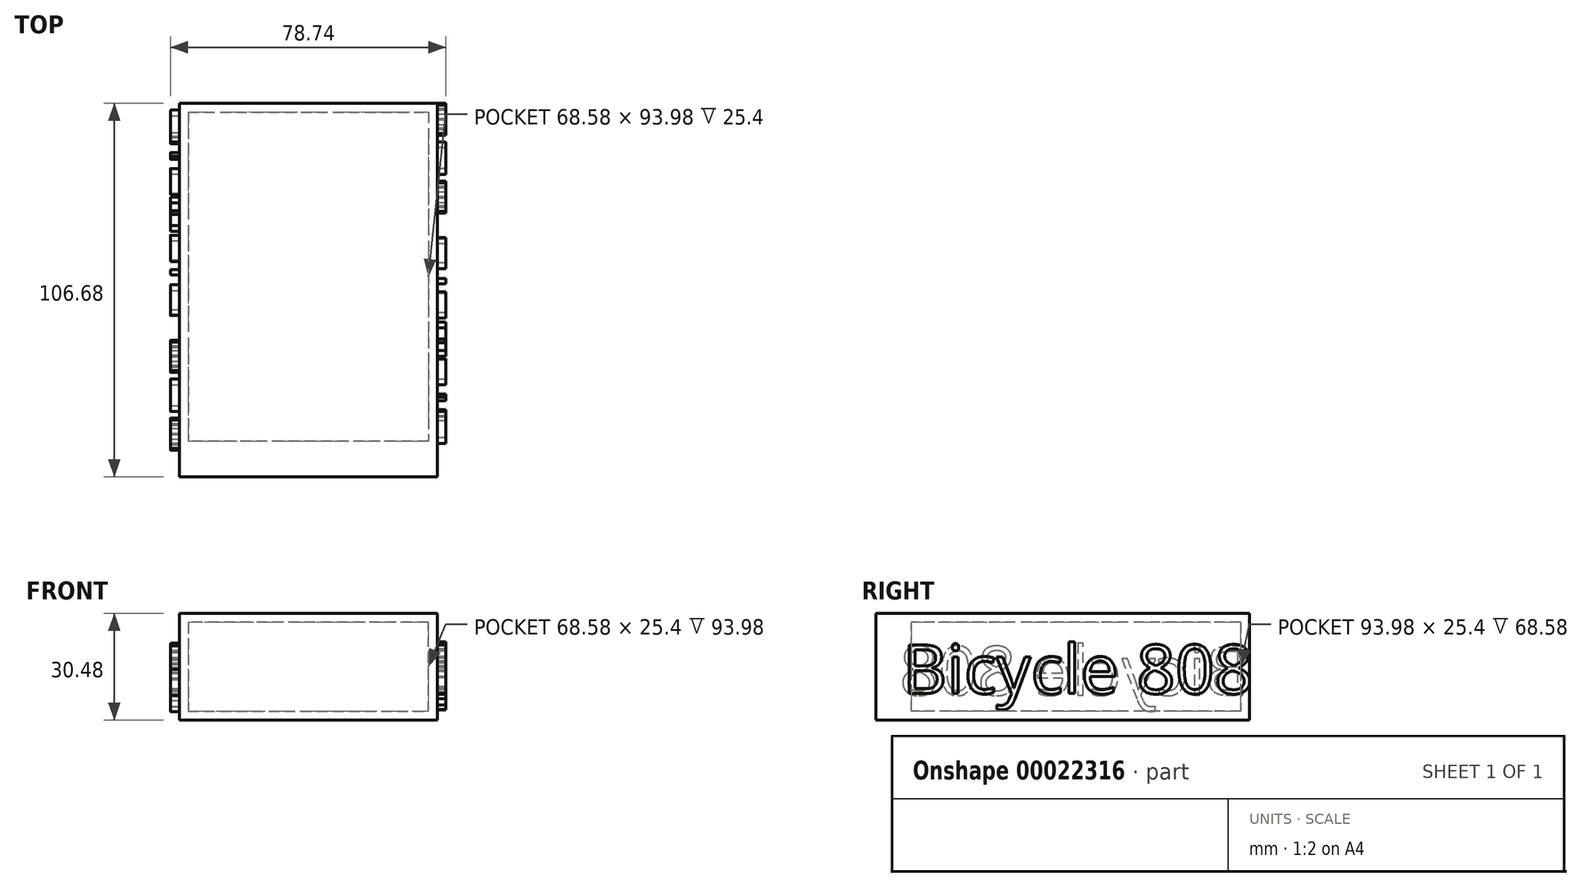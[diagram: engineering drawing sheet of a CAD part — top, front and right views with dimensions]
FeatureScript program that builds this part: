
annotation { "Feature Type Name" : "Feature", "Feature Type Description" : "" }
export const myFeature = defineFeature(function(context is Context, id is Id, definition is map)
    precondition{}
    {
        {
            var Q0;
            Q0=qCreatedBy(makeId("Top.planeOp"),FACE);
            var sketch = newSketch(context, id + "F0", { "sketchPlane" : qUnion([Q0])});
            skLineSegment(sketch, "E0.0", {"start": v(-49.6, -44.56) * mm, "end": v(-49.6, 54.5) * mm});
            skLineSegment(sketch, "E0.2", {"start": v(24.07, -44.56) * mm, "end": v(24.07, 54.5) * mm});
            skLineSegment(sketch, "E0.3", {"start": v(-49.6, 54.5) * mm, "end": v(24.07, 54.5) * mm});
            skLineSegment(sketch, "E1", {"start": v(-49.6, -44.56) * mm, "end": v(24.07, -44.56) * mm});
            skSolve(sketch);
        }
        {
            var Q0;
            Q0 = qSketchRegion(id + "F0", true);
            extrude(context, id + "F1", {"entities" : qUnion([Q0]), "depth" : 30.48 * mm});
        }
        {
            var Q0;
            Q0=makeQuery(id+"F1.opExtrude","SWEPT_FACE",FACE,{"disambiguationData":[OSD([sQuery(id+"F0.wireOp",EDGE,"E1")])]});
            var sketch = newSketch(context, id + "F2", { "sketchPlane" : qUnion([Q0])});
            skLineSegment(sketch, "E2.0", {"start": v(-47.05, 2.54) * mm, "end": v(21.53, 2.54) * mm});
            skLineSegment(sketch, "E2.1", {"start": v(-47.05, 27.94) * mm, "end": v(-47.05, 2.54) * mm});
            skLineSegment(sketch, "E2.2", {"start": v(21.53, 27.94) * mm, "end": v(-47.05, 27.94) * mm});
            skLineSegment(sketch, "E2.3", {"start": v(21.53, 2.54) * mm, "end": v(21.53, 27.94) * mm});
            skSolve(sketch);
        }
        {
            var Q0;
            Q0=makeQuery(id+"F2.imprint","IMPRINT",FACE,{"disambiguationData":[TD([[makeQuery(id+"F2.imprint","IMPRINT",EDGE,{"derivedFrom":sQuery(id+"F2.wireOp",EDGE,"E2.0")}),1.0]])]});
            extrude(context, id + "F3", {"entities" : qUnion([Q0]), "operationType" : NewBodyOperationType.REMOVE, "oppositeDirection" : true, "depth" : 96.52 * mm});
        }
        {
            var Q0;
            Q0=makeQuery(id+"F1.opExtrude","SWEPT_FACE",FACE,{"disambiguationData":[OSD([sQuery(id+"F0.wireOp",EDGE,"E0.2")])]});
            var sketch = newSketch(context, id + "F4", { "sketchPlane" : qUnion([Q0])});
            skText(sketch, "E3", { "text": "Bicycle 808", "fontName": "OpenSans-Regular.ttf"});
            const initialGuessF4  = {"E3": [-0.04456, 0.00759, 1, 0, 0.014]};
            skSetInitialGuess(sketch, initialGuessF4);
            skSolve(sketch);
        }
        {
            var Q0;
            Q0 = qSketchRegion(id + "F4", true);
            extrude(context, id + "F5", {"entities" : qUnion([Q0]), "operationType" : NewBodyOperationType.ADD, "depth" : 2.54 * mm});
        }
        {
            var Q0;
            Q0=makeQuery(id+"F1.opExtrude","SWEPT_FACE",FACE,{"disambiguationData":[OSD([sQuery(id+"F0.wireOp",EDGE,"E0.0")])]});
            var sketch = newSketch(context, id + "F6", { "sketchPlane" : qUnion([Q0])});
            skText(sketch, "E4", { "text": "Bicycle 808", "fontName": "OpenSans-Regular.ttf"});
            const initialGuessF6  = {"E4": [-0.0545, 0.00715, 1, 0, 0.014]};
            skSetInitialGuess(sketch, initialGuessF6);
            skSolve(sketch);
        }
        {
            var Q0;
            Q0 = qSketchRegion(id + "F6", true);
            extrude(context, id + "F7", {"entities" : qUnion([Q0]), "operationType" : NewBodyOperationType.ADD, "depth" : 2.54 * mm});
        }
        {
            var Q0;
            Q0=makeQuery(id+"F1.opExtrude","SWEPT_FACE",FACE,{"disambiguationData":[OSD([sQuery(id+"F0.wireOp",EDGE,"E1")])]});
            var sketch = newSketch(context, id + "F8", { "sketchPlane" : qUnion([Q0])});
            skLineSegment(sketch, "E5.bottom", {"start": v(-49.6, 0) * mm, "end": v(24.07, 0) * mm});
            skLineSegment(sketch, "E5.top", {"start": v(-49.6, 30.48) * mm, "end": v(24.07, 30.48) * mm});
            skLineSegment(sketch, "E5.left", {"start": v(-49.6, 0) * mm, "end": v(-49.6, 30.48) * mm});
            skLineSegment(sketch, "E5.right", {"start": v(24.07, 0) * mm, "end": v(24.07, 30.48) * mm});
            skSolve(sketch);
        }
        {
            var Q0;
            Q0 = qSketchRegion(id + "F8", true);
            extrude(context, id + "F9", {"entities" : qUnion([Q0]), "depth" : 7.62 * mm});
        }
        {
            var Q0;
            Q0=makeQuery(id+"F9.opExtrude","CAP_FACE",FACE,{"disambiguationData":[OSD([sQuery(id+"F8.wireOp",EDGE,"E5.bottom"),sQuery(id+"F8.wireOp",EDGE,"E5.top"),sQuery(id+"F8.wireOp",EDGE,"E5.left"),sQuery(id+"F8.wireOp",EDGE,"E5.right")])],"isStart":false});
            var sketch = newSketch(context, id + "F10", { "sketchPlane" : qUnion([Q0])});
            skLineSegment(sketch, "E6.0", {"start": v(-47.05, 27.94) * mm, "end": v(-47.05, 2.54) * mm});
            skLineSegment(sketch, "E6.1", {"start": v(21.53, 27.94) * mm, "end": v(-47.05, 27.94) * mm});
            skLineSegment(sketch, "E6.2", {"start": v(21.53, 2.54) * mm, "end": v(21.53, 27.94) * mm});
            skLineSegment(sketch, "E6.3", {"start": v(-47.05, 2.54) * mm, "end": v(21.53, 2.54) * mm});
            skSolve(sketch);
        }
        {
            var Q0;
            Q0=makeQuery(id+"F10.imprint","IMPRINT",FACE,{"disambiguationData":[TD([[makeQuery(id+"F10.imprint","IMPRINT",EDGE,{"derivedFrom":sQuery(id+"F10.wireOp",EDGE,"E6.0")}),1.0]])]});
            extrude(context, id + "F11", {"entities" : qUnion([Q0]), "operationType" : NewBodyOperationType.ADD, "oppositeDirection" : true, "depth" : 10.16 * mm});
        }
    });
